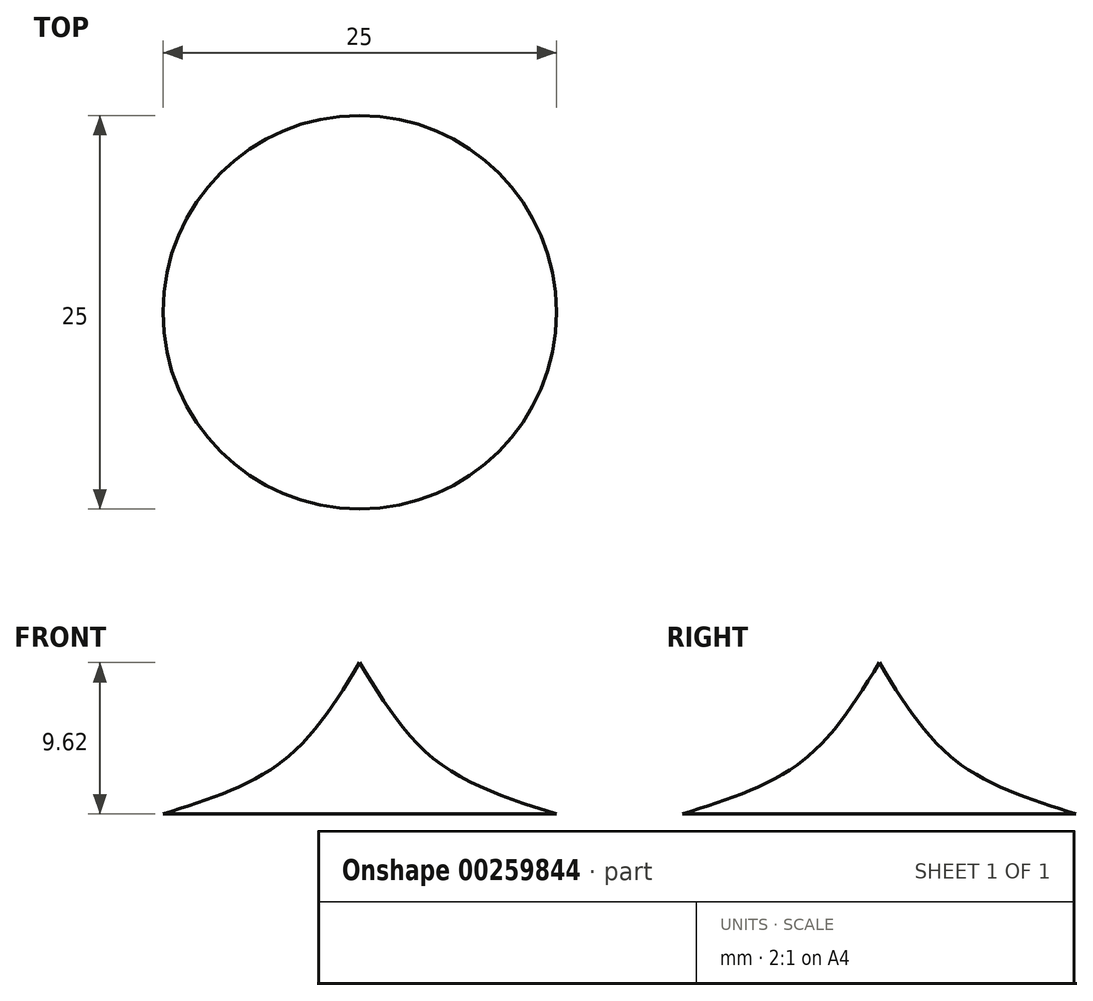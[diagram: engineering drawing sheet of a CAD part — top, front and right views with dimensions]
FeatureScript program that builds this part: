
annotation { "Feature Type Name" : "Feature", "Feature Type Description" : "" }
export const myFeature = defineFeature(function(context is Context, id is Id, definition is map)
    precondition{}
    {
        {
            var Q0;
            Q0=qCreatedBy(makeId("Front.planeOp"),FACE);
            var sketch = newSketch(context, id + "F0", { "sketchPlane" : qUnion([Q0])});
            skLineSegment(sketch, "E0", {"start": v(0, 9.62) * mm, "end": v(0, 0) * mm});
            skLineSegment(sketch, "E1", {"start": v(0, 0) * mm, "end": v(12.5, 0) * mm});
            skFitSpline(sketch, "E2", {"points": [v(12.5, 0) * mm, v(4.85, 3.4) * mm, v(0, 9.62) * mm], "startDerivative": vector(-16.41, 5.18) * mm, "endDerivative": vector(-8.55, 14.1) * mm});
            skLineSegment(sketch, "E3", {"start": v(0, 21.38) * mm, "end": v(0, -9.04) * mm, "construction": true});
            skSolve(sketch);
        }
        {
            var Q0;
            Q0=makeQuery(id+"F0.imprint","IMPRINT",FACE,{"disambiguationData":[TD([[makeQuery(id+"F0.imprint","IMPRINT",EDGE,{"derivedFrom":sQuery(id+"F0.wireOp",EDGE,"E0")}),1.0]])]});
            var Q1;
            Q1=sQuery(id+"F0.wireOp",EDGE,"E3");
            revolve(context, id + "F1", {"entities" : qUnion([Q0]), "axis" : qUnion([Q1]), "revolveType" : RevolveType.FULL});
        }
    });
